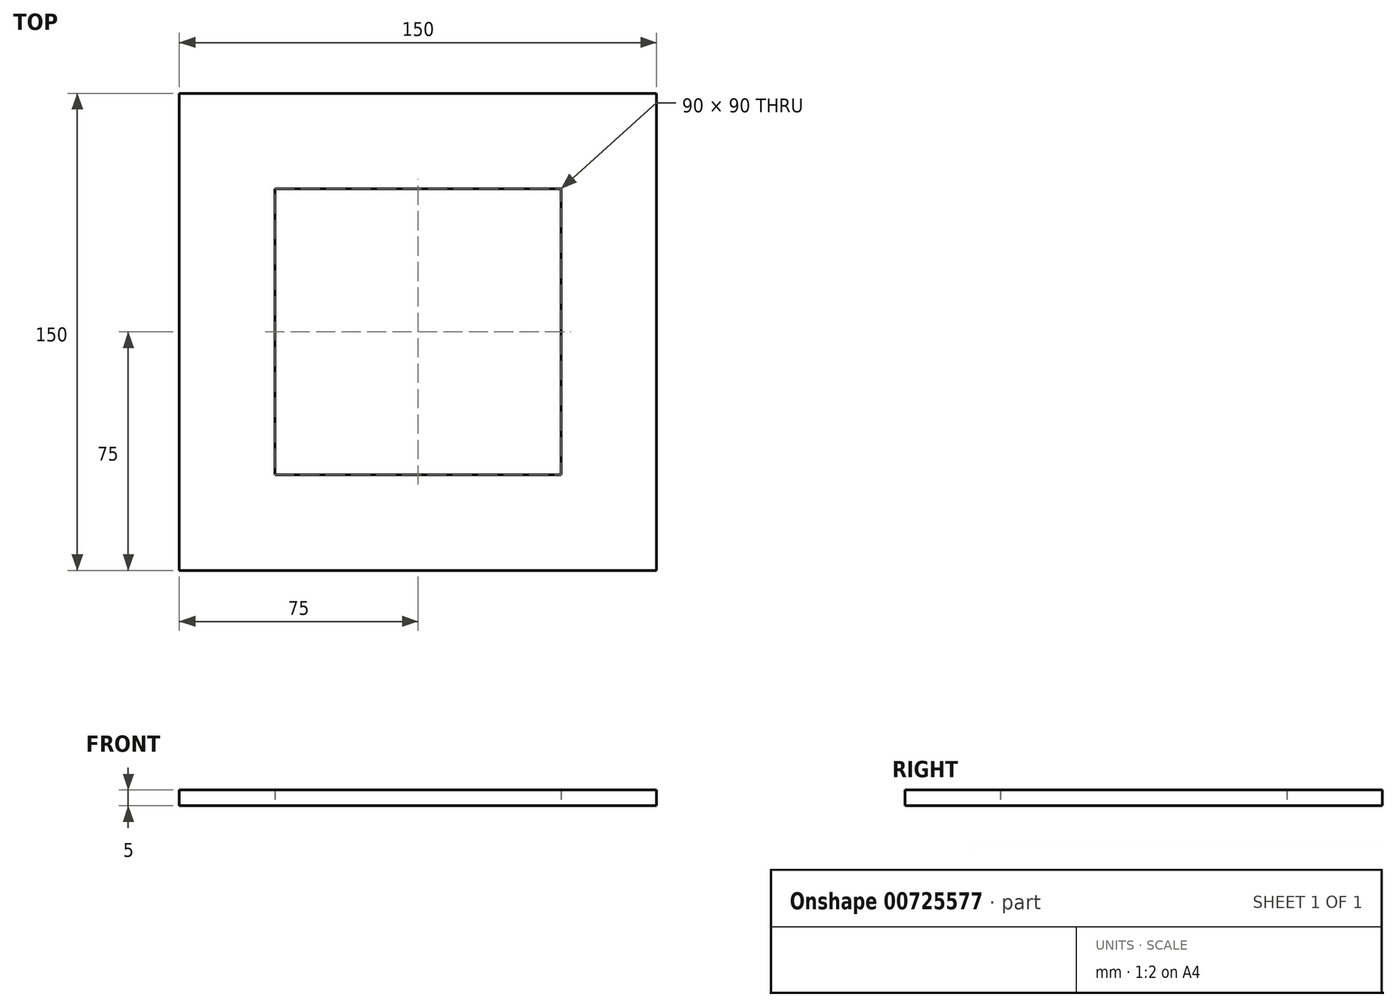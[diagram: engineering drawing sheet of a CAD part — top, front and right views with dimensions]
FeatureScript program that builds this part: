
annotation { "Feature Type Name" : "Feature", "Feature Type Description" : "" }
export const myFeature = defineFeature(function(context is Context, id is Id, definition is map)
    precondition{}
    {
        {
            var Q0;
            Q0=qCreatedBy(makeId("Top.planeOp"),FACE);
            var sketch = newSketch(context, id + "F0", { "sketchPlane" : qUnion([Q0])});
            skLineSegment(sketch, "E0.bottom", {"start": v(-75, -75) * mm, "end": v(75, -75) * mm});
            skLineSegment(sketch, "E0.top", {"start": v(-75, 75) * mm, "end": v(75, 75) * mm});
            skLineSegment(sketch, "E0.left", {"start": v(-75, -75) * mm, "end": v(-75, 75) * mm});
            skLineSegment(sketch, "E0.right", {"start": v(75, -75) * mm, "end": v(75, 75) * mm});
            skLineSegment(sketch, "E1.bottom", {"start": v(-45, -45) * mm, "end": v(45, -45) * mm});
            skLineSegment(sketch, "E1.top", {"start": v(-45, 45) * mm, "end": v(45, 45) * mm});
            skLineSegment(sketch, "E1.left", {"start": v(-45, -45) * mm, "end": v(-45, 45) * mm});
            skLineSegment(sketch, "E1.right", {"start": v(45, -45) * mm, "end": v(45, 45) * mm});
            skLineSegment(sketch, "E2", {"start": v(0, 45) * mm, "end": v(0, 75) * mm, "construction": true});
            skLineSegment(sketch, "E3", {"start": v(45, 0) * mm, "end": v(75, 0) * mm, "construction": true});
            skSolve(sketch);
        }
        {
            var Q0;
            Q0 = qSketchRegion(id + "F0", true);
            extrude(context, id + "F1", {"entities" : qUnion([Q0]), "depth" : 5 * mm, "offsetDistance" : 25 * mm});
        }
    });
